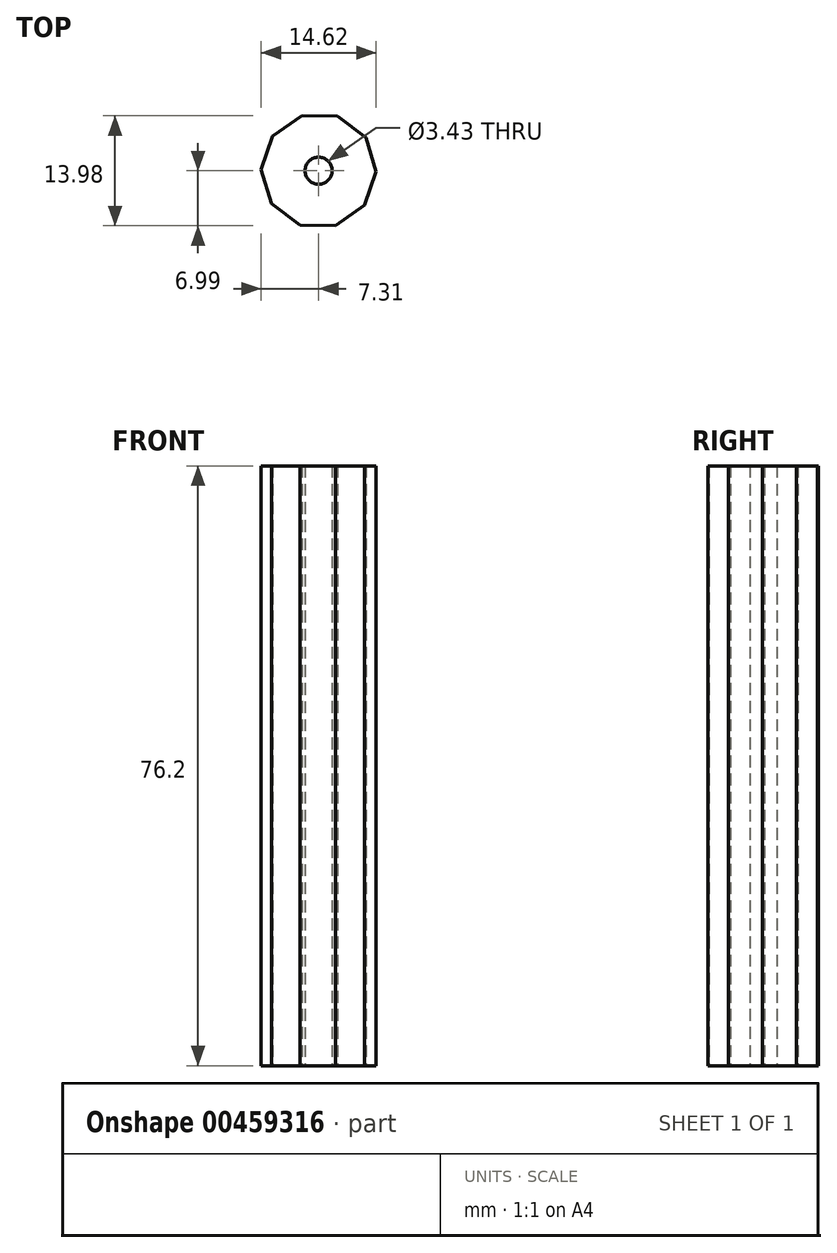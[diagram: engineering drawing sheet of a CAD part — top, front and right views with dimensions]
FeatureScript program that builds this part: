
annotation { "Feature Type Name" : "Feature", "Feature Type Description" : "" }
export const myFeature = defineFeature(function(context is Context, id is Id, definition is map)
    precondition{}
    {
        {
            var Q0;
            Q0=qCreatedBy(makeId("Top.planeOp"),FACE);
            var sketch = newSketch(context, id + "F0", { "sketchPlane" : qUnion([Q0])});
            skCircle(sketch, "E0.cCircle", {"center": v(0, 0) * mm, "radius": 6.95 * mm, "construction": true});
            skLineSegment(sketch, "E0.0", {"start": v(-5.99, -4.2) * mm, "end": v(-2.38, -6.9) * mm});
            skLineSegment(sketch, "E0.1", {"start": v(-7.3, 0.13) * mm, "end": v(-5.99, -4.2) * mm});
            skLineSegment(sketch, "E0.2", {"start": v(-5.84, 4.4) * mm, "end": v(-7.3, 0.13) * mm});
            skLineSegment(sketch, "E0.3", {"start": v(-2.14, 6.99) * mm, "end": v(-5.84, 4.4) * mm});
            skLineSegment(sketch, "E0.4", {"start": v(2.38, 6.9) * mm, "end": v(-2.14, 6.99) * mm});
            skLineSegment(sketch, "E0.5", {"start": v(5.99, 4.2) * mm, "end": v(2.38, 6.9) * mm});
            skLineSegment(sketch, "E0.6", {"start": v(7.3, -0.13) * mm, "end": v(5.99, 4.2) * mm});
            skLineSegment(sketch, "E0.7", {"start": v(5.84, -4.4) * mm, "end": v(7.3, -0.13) * mm});
            skLineSegment(sketch, "E0.8", {"start": v(2.14, -6.99) * mm, "end": v(5.84, -4.4) * mm});
            skLineSegment(sketch, "E0.9", {"start": v(-2.38, -6.9) * mm, "end": v(2.14, -6.99) * mm});
            skPoint(sketch, "E0.0.midPoint", {"position": v(-4.18, -5.55) * mm});
            skSolve(sketch);
        }
        {
            var Q0;
            Q0 = qSketchRegion(id + "F0", true);
            extrude(context, id + "F1", {"entities" : qUnion([Q0]), "depth" : 76.2 * mm});
        }
        {
            var Q0;
            Q0=qCreatedBy(makeId("Top.planeOp"),FACE);
            var sketch = newSketch(context, id + "F2", { "sketchPlane" : qUnion([Q0])});
            skCircle(sketch, "E1", {"center": v(0, 0) * mm, "radius": 1.71 * mm});
            skSolve(sketch);
        }
        {
            var Q0;
            Q0=sQuery(id+"F2.wireOp",VERTEX,"E1.center");
            var Q1;
            Q1=makeQuery(id+"F1.opExtrude","SWEPT_BODY",BODY,{"disambiguationData":[OSD([sQuery(id+"F0.wireOp",EDGE,"E0.0"),sQuery(id+"F0.wireOp",EDGE,"E0.1"),sQuery(id+"F0.wireOp",EDGE,"E0.2"),sQuery(id+"F0.wireOp",EDGE,"E0.3"),sQuery(id+"F0.wireOp",EDGE,"E0.4"),sQuery(id+"F0.wireOp",EDGE,"E0.5"),sQuery(id+"F0.wireOp",EDGE,"E0.6"),sQuery(id+"F0.wireOp",EDGE,"E0.7"),sQuery(id+"F0.wireOp",EDGE,"E0.8"),sQuery(id+"F0.wireOp",EDGE,"E0.9")])]});
            hole(context, id + "F3", {"style" : HoleStyle.SIMPLE, "endStyle" : HoleEndStyle.THROUGH, "oppositeDirection" : true, "holeDiameter" : 3.43 * mm, "isTappedThrough" : true, "tappedDepth" : 12.7 * mm, "tapClearance" : 3, "locations" : qUnion([Q0]), "scope" : qUnion([Q1])});
        }
    });
